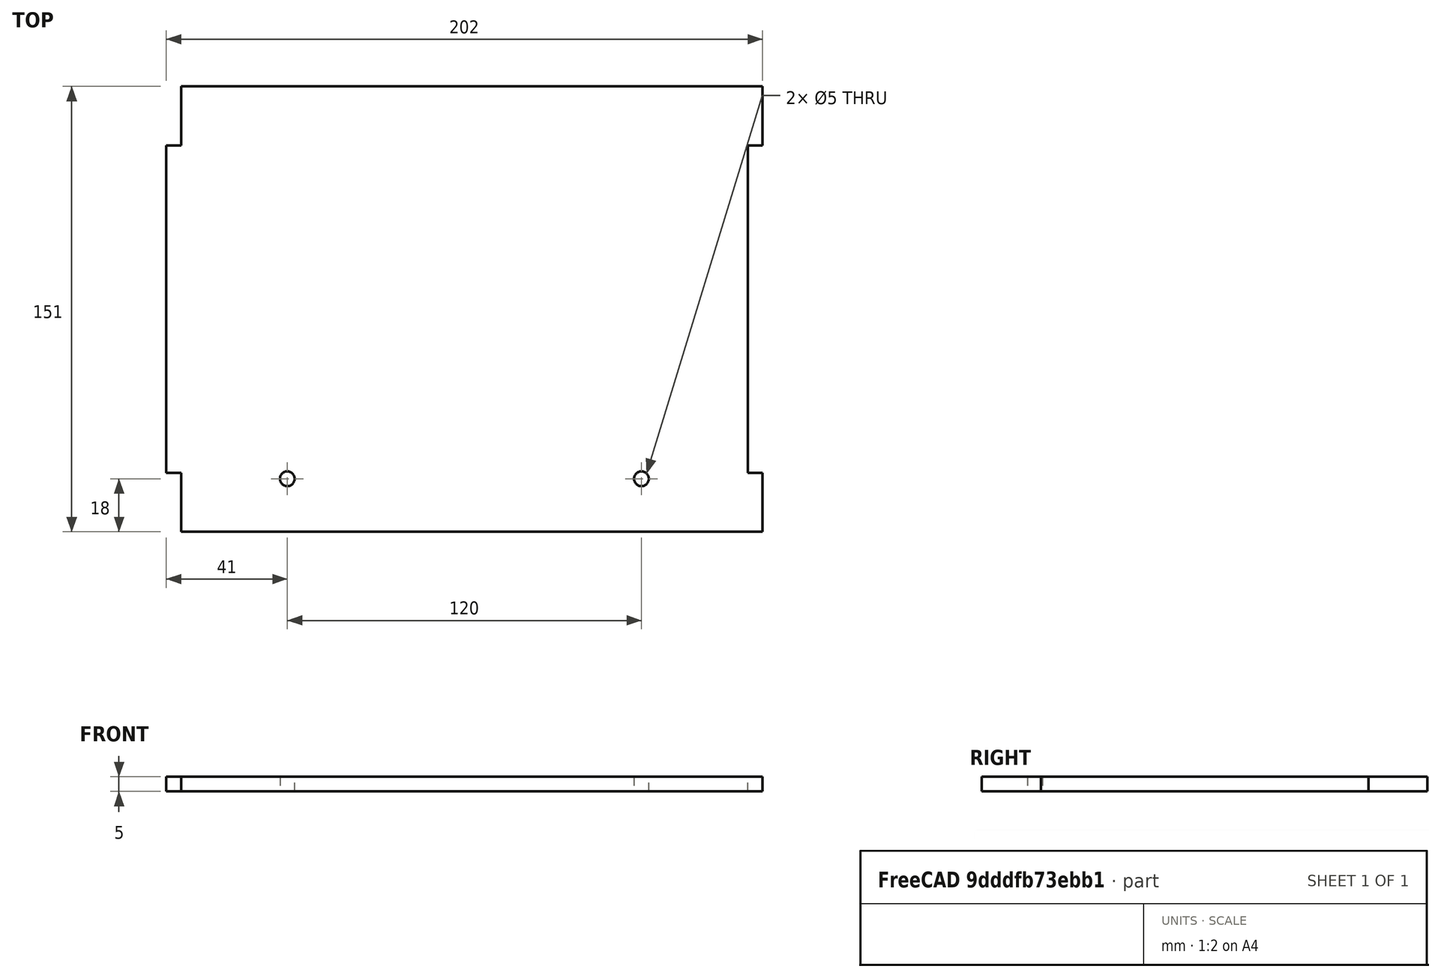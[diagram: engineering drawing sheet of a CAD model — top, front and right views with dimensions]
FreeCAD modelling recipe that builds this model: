
FCSTD DOCUMENT  (FreeCAD 0.15R4671 (Git))
Label: upper_side_axis_x2
License: All rights reserved
LicenseURL: http://en.wikipedia.org/wiki/All_rights_reserved
objects: Sketcher::SketchObject×1, PartDesign::Pad×1
note: 3 computed .brp shape members not serialized (recipe doc carries the construction recipe); baked Part::Feature solids carry a one-line shape summary decoded from their .brp

FEATURE [Sketcher::SketchObject] Sketch
  sketch-geometry (15):
    g0: LineSegment StartX=98.5 StartY=55.5 StartZ=0 EndX=98.5 EndY=75.5 EndZ=0
    g1: LineSegment StartX=98.5 StartY=75.5 StartZ=0 EndX=-98.5 EndY=75.5 EndZ=0
    g2: LineSegment StartX=-98.5 StartY=75.5 StartZ=0 EndX=-98.5 EndY=55.5 EndZ=0
    g3: LineSegment StartX=-98.5 StartY=55.5 StartZ=0 EndX=-103.5 EndY=55.5 EndZ=0
    g4: LineSegment StartX=-103.5 StartY=55.5 StartZ=0 EndX=-103.5 EndY=-55.5 EndZ=0
    g5: LineSegment StartX=-103.5 StartY=-55.5 StartZ=0 EndX=-98.5 EndY=-55.5 EndZ=0
    g6: LineSegment StartX=-98.5 StartY=-55.5 StartZ=0 EndX=-98.5 EndY=-75.5 EndZ=0
    g7: LineSegment StartX=-98.5 StartY=-75.5 StartZ=0 EndX=98.5 EndY=-75.5 EndZ=0
    g8: LineSegment StartX=98.5 StartY=-75.5 StartZ=0 EndX=98.5 EndY=-55.5 EndZ=0
    g9: LineSegment StartX=98.5 StartY=-55.5 StartZ=0 EndX=93.5 EndY=-55.5 EndZ=0
    g10: LineSegment StartX=93.5 StartY=-55.5 StartZ=0 EndX=93.5 EndY=55.5 EndZ=0
    g11: LineSegment StartX=93.5 StartY=55.5 StartZ=0 EndX=98.5 EndY=55.5 EndZ=0
    g12: Circle CenterX=57.5 CenterY=-57.5 CenterZ=0 NormalX=0 NormalY=0 NormalZ=1 Radius=2.5
    g13: Circle CenterX=-62.5 CenterY=-57.5 CenterZ=0 NormalX=0 NormalY=0 NormalZ=1 Radius=2.5
    g14: LineSegment [constr] StartX=-62.5 StartY=-57.5 StartZ=0 EndX=57.5 EndY=-57.5 EndZ=0
  constraints (44):
    c: Coincident(g3,g4)
    c: Coincident(g2,g3)
    c: Coincident(g1,g2)
    c: Coincident(g0,g1)
    c: Coincident(g0,g11)
    c: Coincident(g10,g11)
    c: Coincident(g9,g10)
    c: Coincident(g8,g9)
    c: Coincident(g7,g8)
    c: Coincident(g6,g7)
    c: Coincident(g5,g6)
    c: Coincident(g4,g5)
    c: Vertical(g4)
    c: Vertical(g2)
    c: Vertical(g0)
    c: Vertical(g10)
    c: Vertical(g8)
    c: Vertical(g6)
    c: Horizontal(g3)
    c: Horizontal(g5)
    c: Horizontal(g9)
    c: Horizontal(g11)
    c: Horizontal(g1)
    c: Horizontal(g7)
    c: Equal(g3,g5)
    c: Equal(g5,g9)
    c: Equal(g9,g11)
    c: DistanceX(g11) = 5
    c: Equal(g2,g6)
    c: Equal(g6,g8)
    c: Equal(g8,g0)
    c: DistanceY(g1,g6) = -151
    c: DistanceY(g4) = -111
    c: DistanceX(g10,g2) = -192
    c: Equal(g13,g12)
    c: Radius(g12) = 2.5
    c: DistanceX(g13,g5) = -36
    c: DistanceY(g13,g6) = -18
    c: DistanceX(g12,g9) = 36
    c: Coincident(g14,g13)
    c: Coincident(g14,g12)
    c: Horizontal(g14)
    c: Symmetric(g0,g7,g-1)
    c: Symmetric(g1,g0,g-2)
FEATURE [PartDesign::Pad] Pad
  Length = 5
  Length2 = 100
  Midplane = true
  Sketch = -> Sketch
  Type = 0
